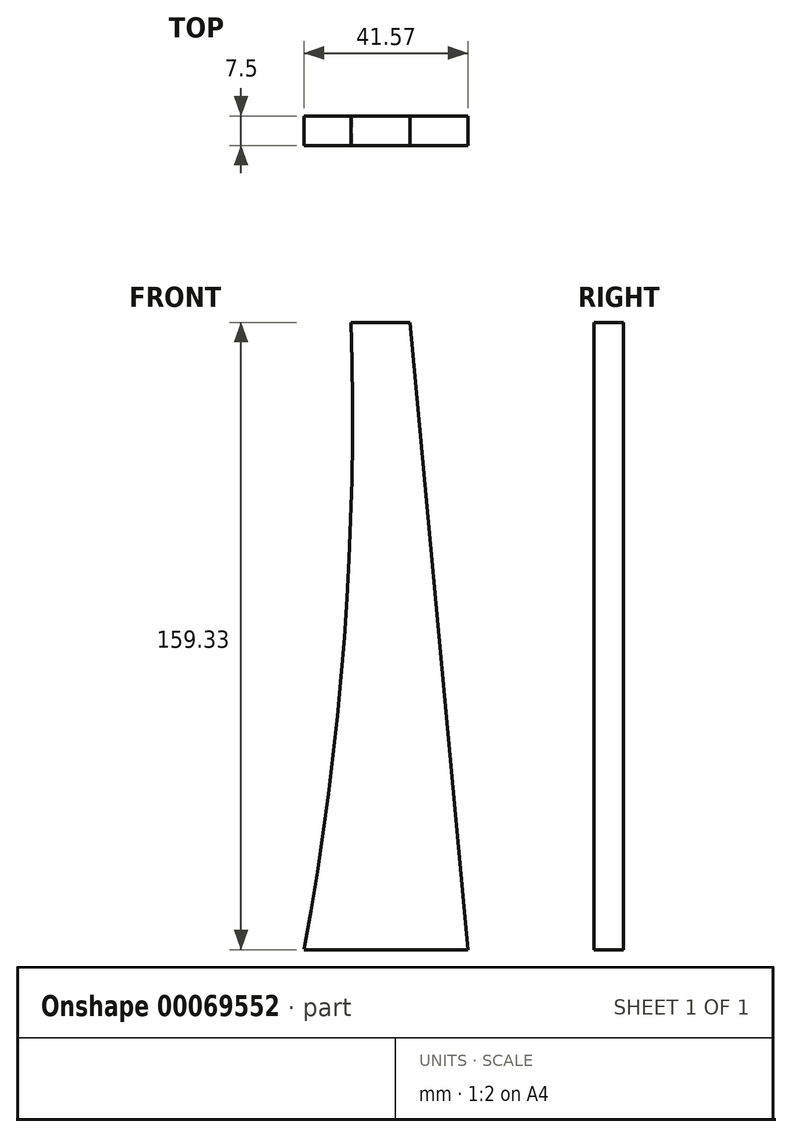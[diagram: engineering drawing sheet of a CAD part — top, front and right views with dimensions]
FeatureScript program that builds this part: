
annotation { "Feature Type Name" : "Feature", "Feature Type Description" : "" }
export const myFeature = defineFeature(function(context is Context, id is Id, definition is map)
    precondition{}
    {
        {
            var Q0;
            Q0=qCreatedBy(makeId("Front.planeOp"),FACE);
            var sketch = newSketch(context, id + "F0", { "sketchPlane" : qUnion([Q0])});
            skLineSegment(sketch, "E0", {"start": v(-9.25, 94.29) * mm, "end": v(5.75, 94.29) * mm});
            skLineSegment(sketch, "E1", {"start": v(5.75, 94.29) * mm, "end": v(20.45, -65.04) * mm});
            skArc(sketch, "E2", {"start": v(-21.12, -65.04) * mm, "mid": v(-10.91, 14.3) * mm, "end": v(-9.25, 94.29) * mm});
            skLineSegment(sketch, "E3", {"start": v(-4.72, -85) * mm, "end": v(15.28, -85) * mm});
            skArc(sketch, "E4", {"start": v(-4.72, -85) * mm, "mid": v(-12.38, -74.57) * mm, "end": v(-21.12, -65.04) * mm});
            skLineSegment(sketch, "E5", {"start": v(20.45, -65.04) * mm, "end": v(15.28, -85) * mm});
            skLineSegment(sketch, "E6", {"start": v(-21.12, -65.04) * mm, "end": v(20.45, -65.04) * mm});
            skSolve(sketch);
        }
        {
            var Q0;
            Q0=makeQuery(id+"F0.imprint","IMPRINT",FACE,{"disambiguationData":[TD([[makeQuery(id+"F0.imprint","IMPRINT",EDGE,{"derivedFrom":sQuery(id+"F0.wireOp",EDGE,"E0")}),-1.0]])]});
            extrude(context, id + "F1", {"entities" : qUnion([Q0]), "depth" : 7.5 * mm});
        }
    });
